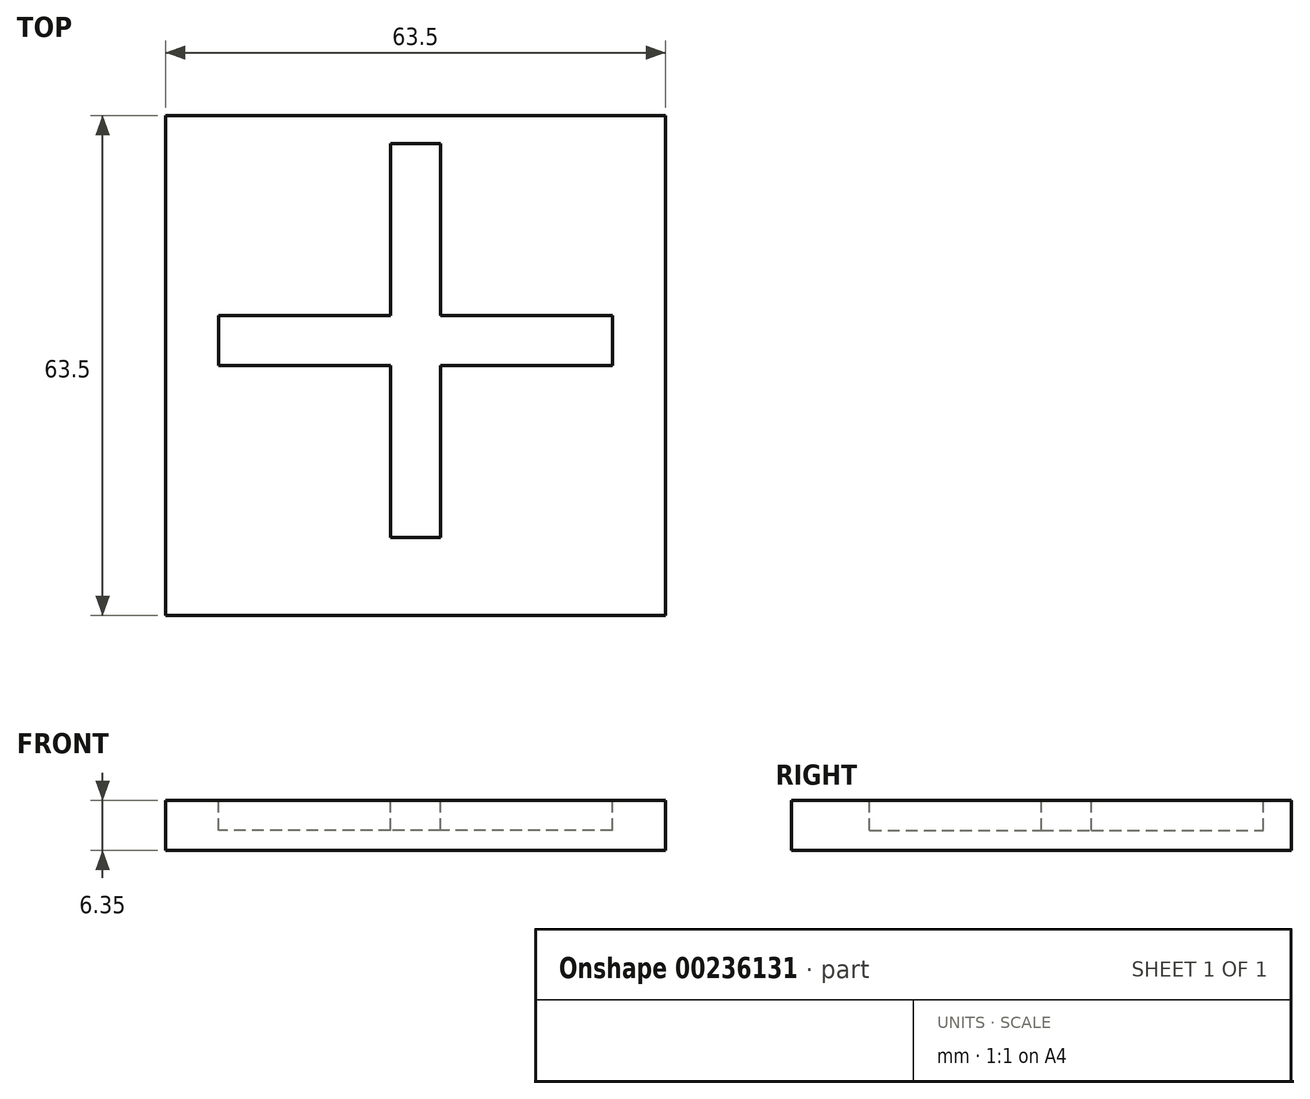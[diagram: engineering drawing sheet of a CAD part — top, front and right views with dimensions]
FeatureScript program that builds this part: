
annotation { "Feature Type Name" : "Feature", "Feature Type Description" : "" }
export const myFeature = defineFeature(function(context is Context, id is Id, definition is map)
    precondition{}
    {
        {
            var Q0;
            Q0=qCreatedBy(makeId("Top.planeOp"),FACE);
            var sketch = newSketch(context, id + "F0", { "sketchPlane" : qUnion([Q0])});
            skLineSegment(sketch, "E0.bottom", {"start": v(-31.75, 31.75) * mm, "end": v(31.75, 31.75) * mm});
            skLineSegment(sketch, "E0.top", {"start": v(-31.75, -31.75) * mm, "end": v(31.75, -31.75) * mm});
            skLineSegment(sketch, "E0.left", {"start": v(-31.75, 31.75) * mm, "end": v(-31.75, -31.75) * mm});
            skLineSegment(sketch, "E0.right", {"start": v(31.75, 31.75) * mm, "end": v(31.75, -31.75) * mm});
            skPoint(sketch, "E0.middle", {"position": v(0, 0) * mm});
            skSolve(sketch);
        }
        {
            var Q0;
            Q0 = qSketchRegion(id + "F0", true);
            extrude(context, id + "F1", {"entities" : qUnion([Q0]), "depth" : 6.35 * mm});
        }
        {
            var Q0;
            Q0=makeQuery(id+"F1.opExtrude","CAP_FACE",FACE,{"disambiguationData":[OSD([sQuery(id+"F0.wireOp",EDGE,"E0.bottom"),sQuery(id+"F0.wireOp",EDGE,"E0.top"),sQuery(id+"F0.wireOp",EDGE,"E0.left"),sQuery(id+"F0.wireOp",EDGE,"E0.right")])],"isStart":false});
            var sketch = newSketch(context, id + "F2", { "sketchPlane" : qUnion([Q0])});
            skLineSegment(sketch, "E1.bottom", {"start": v(25, 0) * mm, "end": v(-25, 0) * mm});
            skLineSegment(sketch, "E1.top", {"start": v(25, 6.35) * mm, "end": v(-25, 6.35) * mm});
            skLineSegment(sketch, "E1.left", {"start": v(25, 0) * mm, "end": v(25, 6.35) * mm});
            skLineSegment(sketch, "E1.right", {"start": v(-25, 0) * mm, "end": v(-25, 6.35) * mm});
            skPoint(sketch, "E1.middle", {"position": v(0, 3.18) * mm});
            skLineSegment(sketch, "E2.bottom", {"start": v(3.18, -21.83) * mm, "end": v(-3.17, -21.83) * mm});
            skLineSegment(sketch, "E2.top", {"start": v(3.18, 28.17) * mm, "end": v(-3.17, 28.17) * mm});
            skLineSegment(sketch, "E2.left", {"start": v(3.18, -21.82) * mm, "end": v(3.18, 28.18) * mm});
            skLineSegment(sketch, "E2.right", {"start": v(-3.17, -21.83) * mm, "end": v(-3.17, 28.17) * mm});
            skSolve(sketch);
        }
        {
            var Q0;
            Q0 = qSketchRegion(id + "F2", true);
            extrude(context, id + "F3", {"entities" : qUnion([Q0]), "operationType" : NewBodyOperationType.REMOVE, "oppositeDirection" : true, "depth" : 3.8 * mm});
        }
    });
